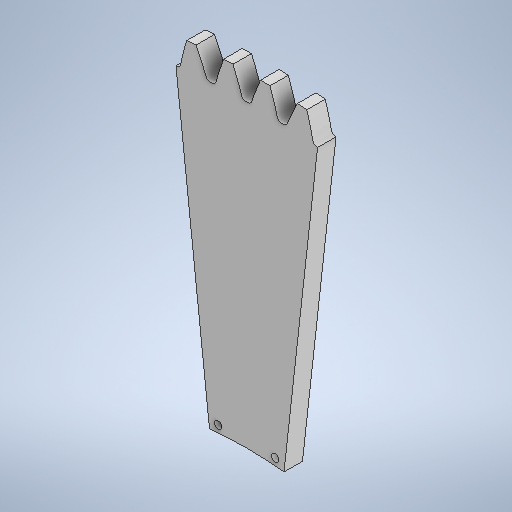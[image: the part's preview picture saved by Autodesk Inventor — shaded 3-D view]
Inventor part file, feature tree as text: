
AUTODESK INVENTOR PART (.ipt)
format: ipt  version: 2025 (Build 290162010, 162A)  size: 797,696 bytes
history: native  units: mm
features: extrude x3, sketch x2, pattern_circular x1, hole x1, projected_geometry x1
ambient origin geometry x8: Origin, YZ Plane, XZ Plane, XY Plane, X Axis, Y Axis, Z Axis, Center Point
bodies: Solid1 (feature_tree)
feature tree (8):
  extrude  "Extrusion1"  TaperAngle=0.0deg  [1 undecoded]
  extrude  "Extrusion2"  Depth=4.0mm TaperAngle=360.0deg
  pattern_circular  "Circular Pattern1"  Count=72  [1 undecoded]
  extrude  "Extrusion3"  Depth=4.0mm
  hole  "Hole1"  [1 undecoded]
  sketch  "Sketch2"  dims[d0=20.0mm d1=0.0mm]
  projected_geometry  "Projected Loop1"
  sketch  "Sketch3"  dims[d2=0.0mm d3=0.0mm d4=1120.0mm d5=360.0deg d7=720.0mm d8=2.243998mm d9=0.0mm d10=0.0mm d11=735.0mm d12=1.68337mm d13=8.0mm d14=6.0mm d15=4.0mm d16=2.0mm d17=90.0deg d18=8.0mm d19=20.594885mm]
note: 3 required parameter values undecoded (feature->parameter linkage not recoverable at this tier; creation-order binding heuristic only, values carry confidence <= 0.55)
